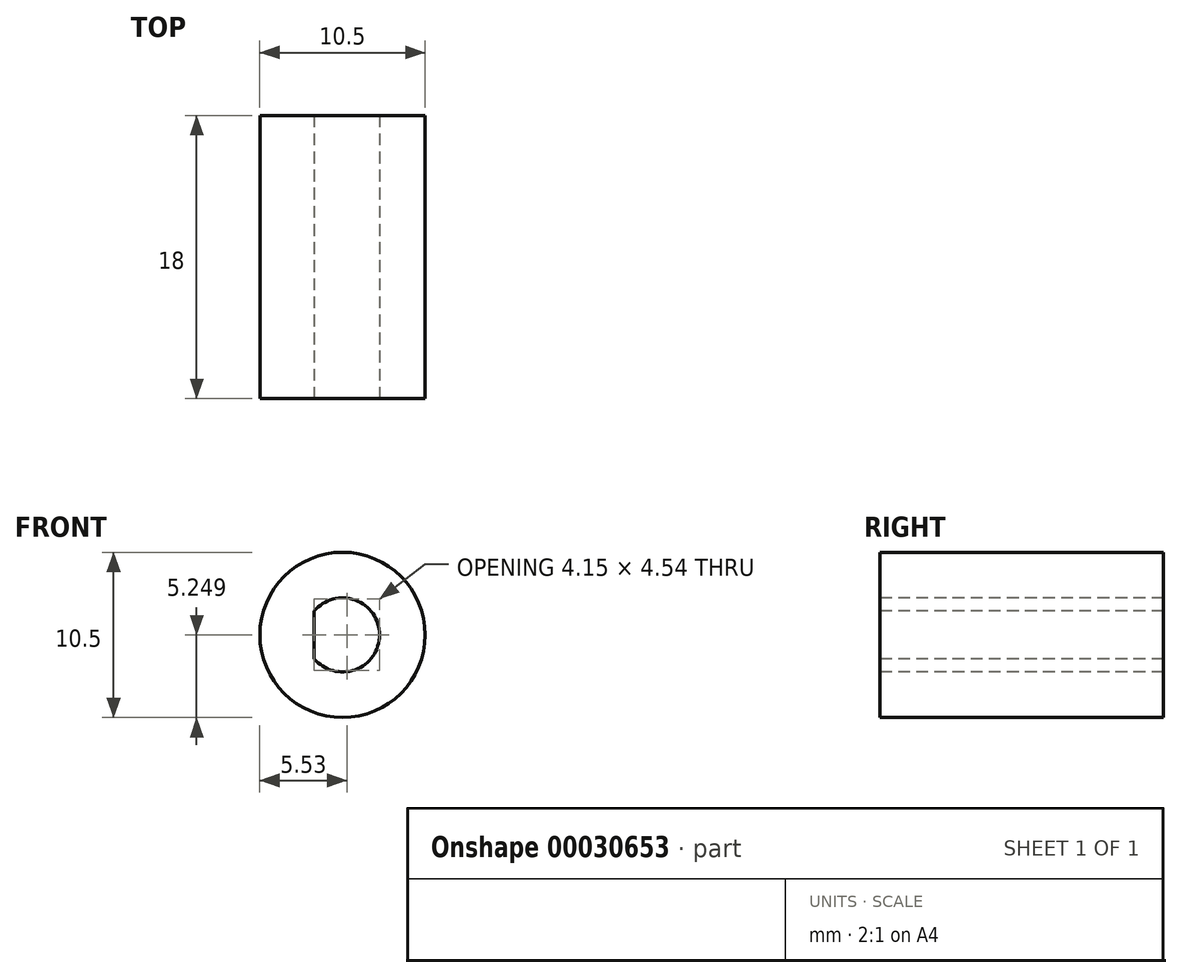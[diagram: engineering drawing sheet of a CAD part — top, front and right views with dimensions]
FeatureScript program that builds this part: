
annotation { "Feature Type Name" : "Feature", "Feature Type Description" : "" }
export const myFeature = defineFeature(function(context is Context, id is Id, definition is map)
    precondition{}
    {
        {
            var Q0;
            Q0=qCreatedBy(makeId("Front.planeOp"),FACE);
            var sketch = newSketch(context, id + "F0", { "sketchPlane" : qUnion([Q0])});
            skCircle(sketch, "E0", {"center": v(-1.8, 2.56) * mm, "radius": 5.25 * mm});
            skSolve(sketch);
        }
        {
            var Q0;
            Q0=makeQuery(id+"F0.imprint","IMPRINT",FACE,{"disambiguationData":[TD([[makeQuery(id+"F0.imprint","IMPRINT",EDGE,{"derivedFrom":sQuery(id+"F0.wireOp",EDGE,"E0")}),1.0]])]});
            extrude(context, id + "F1", {"entities" : qUnion([Q0]), "depth" : 18 * mm});
        }
        {
            var Q0;
            Q0=makeQuery(id+"F1.opExtrude","CAP_FACE",FACE,{"disambiguationData":[OSD([sQuery(id+"F0.wireOp",EDGE,"E0")])],"isStart":false});
            var sketch = newSketch(context, id + "F2", { "sketchPlane" : qUnion([Q0])});
            skArc(sketch, "E1", {"start": v(-3.6, 1.05) * mm, "mid": v(0.55, 2.56) * mm, "end": v(-3.6, 4.07) * mm});
            skLineSegment(sketch, "E2", {"start": v(-3.6, 4.07) * mm, "end": v(-3.6, 1.05) * mm});
            skSolve(sketch);
        }
        {
            var Q0;
            Q0=makeQuery(id+"F2.imprint","IMPRINT",FACE,{"disambiguationData":[TD([[makeQuery(id+"F2.imprint","IMPRINT",EDGE,{"derivedFrom":sQuery(id+"F2.wireOp",EDGE,"E1")}),1.0]])]});
            var Q1;
            Q1=makeQuery(id+"F1.opExtrude","CAP_FACE",FACE,{"disambiguationData":[OSD([sQuery(id+"F0.wireOp",EDGE,"E0")])],"isStart":true});
            extrude(context, id + "F3", {"entities" : qUnion([Q0]), "operationType" : NewBodyOperationType.REMOVE, "endBound" : BoundingType.UP_TO_SURFACE, "oppositeDirection" : true, "endBoundEntityFace" : qUnion([Q1]), "depth" : 25 * mm});
        }
    });
